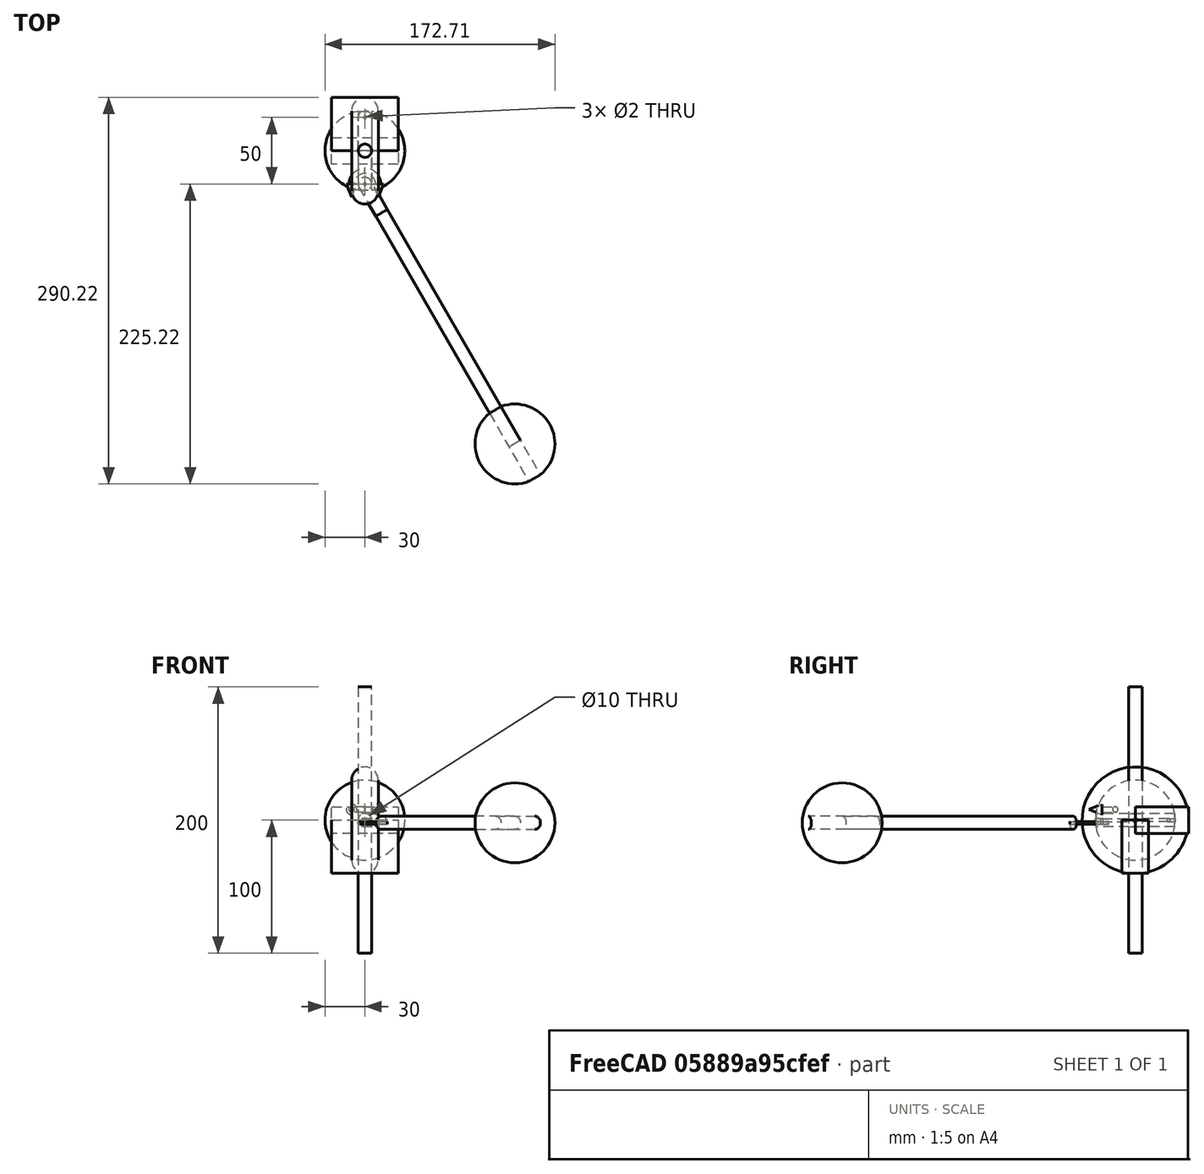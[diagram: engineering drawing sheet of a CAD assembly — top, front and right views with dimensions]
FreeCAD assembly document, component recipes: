
FREECAD ASSEMBLY — COMPONENT RECIPES ("NikraDAPBeginnersTutorial3")

This assembly document has 7 components, labeled P0..P6 below (a component is one placed body or linked part). 6 of them carry a construction recipe — the FreeCAD feature program that regenerates the part from scratch, quoted from this document or its linked companion documents; the rest are supplied as boundary geometry only. No exploded tour is included for this assembly.
COMPONENT P0 — recipe-attached ("LugBody", modeled in this document).
Construction recipe (the document's own serialized feature program — sketch geometry with constraints, then the solid features built on it; lengths are millimeters unless a unit is written):

FEATURE [Sketcher::SketchObject] Sketch
  FullyConstrained = true
  MapMode = 5
  Support = -> [XY_Plane]
  sketch-geometry (5):
    g0: LineSegment StartX=-5 StartY=0 StartZ=0 EndX=-5 EndY=25 EndZ=0
    g1: LineSegment StartX=5 StartY=25 StartZ=0 EndX=5 EndY=0 EndZ=0
    g2: LineSegment StartX=5 StartY=0 StartZ=0 EndX=-5 EndY=0 EndZ=0
    g3: Circle CenterX=0 CenterY=25 CenterZ=0 NormalX=0 NormalY=0 NormalZ=1 AngleXU=0 Radius=1
    g4: ArcOfCircle CenterX=0 CenterY=25 CenterZ=0 NormalX=0 NormalY=0 NormalZ=1 AngleXU=0 Radius=5 StartAngle=5e-16 EndAngle=3.1416
  constraints (13):
    c: PointOnObject(g0,g-1)
    c: Vertical(g0)
    c: Coincident(g1,g2)
    c: Coincident(g2,g0)
    c: Vertical(g1)
    c: Symmetric(g0,g1,g-1)
    c: Radius(g3) = 1
    c: Distance(g1) = 25
    c: Coincident(g4,g3)
    c: Coincident(g4,g0)
    c: Radius(g4) = 5
    c: Tangent(g4,g1) = 1.5708
    c: PointOnObject(g3,g-2)
FEATURE [PartDesign::Pad] Pad004
  Direction = (0,0,1)
  Length = 2
  Length2 = 10
  Midplane = true
  Profile = -> Sketch
  ReferenceAxis = -> Sketch [N_Axis]
  Type = 0
FEATURE [PartDesign::CoordinateSystem] LugFace
  AttacherType = Attacher::AttachEngine3D
  MapMode = 5
  Placement = pos=(0,0,0) rot=(1,0,0;1.5708rad)
  Support = -> [Pad004]
FEATURE [PartDesign::CoordinateSystem] LugHole
  AttacherType = Attacher::AttachEngine3D
  MapMode = 11
  Placement = pos=(0,25,1) rot=(0,0,1;1.5708rad)
  Support = -> [Pad004]
FEATURE [PartDesign::CoordinateSystem] LugHoleRot
  AttacherType = Attacher::AttachEngine3D
  AttachmentOffset = pos=(0,0,0) rot=(0,0,1;0.523599rad)
  MapMode = 11
  Placement = pos=(0,25,1) rot=(0,0,1;2.0944rad)
  Support = -> [Pad004]
FEATURE [PartDesign::Body] Body  label="LugBody"
  Group = -> [Sketch,Pad004,LugFace,LugHole,LugHoleRot]
  Origin = -> Origin
  Tip = -> Pad004
COMPONENT P1 — recipe-attached ("RodBody", modeled in this document).
Construction recipe (the document's own serialized feature program — sketch geometry with constraints, then the solid features built on it; lengths are millimeters unless a unit is written):

FEATURE [Sketcher::SketchObject] Sketch001
  FullyConstrained = true
  MapMode = 5
  Support = -> [XY_Plane001]
  sketch-geometry (1):
    g0: Circle CenterX=0 CenterY=0 CenterZ=0 NormalX=0 NormalY=0 NormalZ=1 AngleXU=0 Radius=5
  constraints (2):
    c: Coincident(g0,g-1)
    c: Radius(g0) = 5
FEATURE [PartDesign::Pad] Pad
  Direction = (0,0,1)
  Length = 200
  Length2 = 10
  Midplane = true
  Profile = -> Sketch001
  ReferenceAxis = -> Sketch001 [N_Axis]
  Type = 0
FEATURE [PartDesign::CoordinateSystem] RodTop
  AttacherType = Attacher::AttachEngine3D
  MapMode = 11
  Placement = pos=(0,0,100) rot=(0,0,1;1.5708rad)
  Support = -> [Pad]
FEATURE [PartDesign::CoordinateSystem] RodBot
  AttacherType = Attacher::AttachEngine3D
  MapMode = 11
  Placement = pos=(0,0,-100) rot=(0,0,1;1.5708rad)
  Support = -> [Pad]
FEATURE [PartDesign::Body] Body001  label="RodBody"
  Group = -> [Sketch001,Pad,RodTop,RodBot]
  Origin = -> Origin001
  Tip = -> Pad
COMPONENT P2 — recipe-attached ("BobBody", modeled in this document).
Construction recipe (the document's own serialized feature program — sketch geometry with constraints, then the solid features built on it; lengths are millimeters unless a unit is written):

FEATURE [Sketcher::SketchObject] Sketch004
  FullyConstrained = true
  MapMode = 5
  Support = -> [XY_Plane004]
  sketch-geometry (4):
    g0: LineSegment StartX=-10 StartY=0 StartZ=0 EndX=-10 EndY=30 EndZ=0
    g1: ArcOfCircle CenterX=0 CenterY=30 CenterZ=0 NormalX=0 NormalY=0 NormalZ=1 AngleXU=0 Radius=10 StartAngle=2e-16 EndAngle=3.14159
    g2: LineSegment StartX=10 StartY=30 StartZ=0 EndX=10 EndY=0 EndZ=0
    g3: LineSegment StartX=10 StartY=0 StartZ=0 EndX=-10 EndY=0 EndZ=0
  constraints (11):
    c: PointOnObject(g0,g-1)
    c: Vertical(g0)
    c: Tangent(g0,g1) = 1.5708
    c: Tangent(g1,g2) = 1.5708
    c: Coincident(g2,g3)
    c: Coincident(g3,g0)
    c: Vertical(g2)
    c: PointOnObject(g1,g-2)
    c: Diameter(g1) = 20
    c: Distance(g0) = 30
    c: PointOnObject(g2,g-1)
FEATURE [PartDesign::Revolution] Revolution001
  Angle = 360
  Axis = (1,0,0)
  Base = (0,0,0)
  Profile = -> Sketch004
  ReferenceAxis = -> Sketch004 [H_Axis]
FEATURE [PartDesign::CoordinateSystem] BobSurface
  AttacherType = Attacher::AttachEngine3D
  MapMode = 11
  Placement = pos=(10,-3.6e-15,0) rot=(0.707107,0,0.707107;3.14159rad)
  Support = -> [Revolution001]
FEATURE [PartDesign::Body] Body004  label="BobBody"
  Group = -> [Sketch004,Revolution001,BobSurface]
  Origin = -> Origin004
  Tip = -> Revolution001
COMPONENT P3 — recipe-attached ("GroundBody", modeled in this document).
Construction recipe (the document's own serialized feature program — sketch geometry with constraints, then the solid features built on it; lengths are millimeters unless a unit is written):

FEATURE [Sketcher::SketchObject] Sketch005
  FullyConstrained = true
  MapMode = 5
  Support = -> [XY_Plane005]
  sketch-geometry (4):
    g0: LineSegment StartX=-25 StartY=10 StartZ=0 EndX=25 EndY=10 EndZ=0
    g1: LineSegment StartX=25 StartY=10 StartZ=0 EndX=25 EndY=-10 EndZ=0
    g2: LineSegment StartX=25 StartY=-10 StartZ=0 EndX=-25 EndY=-10 EndZ=0
    g3: LineSegment StartX=-25 StartY=-10 StartZ=0 EndX=-25 EndY=10 EndZ=0
  constraints (11):
    c: Coincident(g0,g1)
    c: Coincident(g1,g2)
    c: Coincident(g2,g3)
    c: Coincident(g3,g0)
    c: Horizontal(g0)
    c: Horizontal(g2)
    c: Vertical(g1)
    c: Vertical(g3)
    c: DistanceY(g2,g0) = 20
    c: DistanceX(g0,g0) = 50
    c: Symmetric(g0,g1,g-1)
FEATURE [PartDesign::Pad] Pad003
  Direction = (0,0,1)
  Length = 40
  Length2 = 10
  Profile = -> Sketch005
  ReferenceAxis = -> Sketch005 [N_Axis]
  Reversed = true
  Type = 0
FEATURE [PartDesign::CoordinateSystem] GroundFace
  AttacherType = Attacher::AttachEngine3D
  MapMode = 5
  Support = -> [Pad003]
FEATURE [PartDesign::Body] Body005  label="GroundBody"
  Group = -> [Sketch005,Pad003,GroundFace]
  Origin = -> Origin005
  Tip = -> Pad003
COMPONENT P4 — recipe-attached ("ShortRodBody", modeled in this document).
Construction recipe (the document's own serialized feature program — sketch geometry with constraints, then the solid features built on it; lengths are millimeters unless a unit is written):

FEATURE [Sketcher::SketchObject] Sketch006
  FullyConstrained = true
  MapMode = 5
  Support = -> [XY_Plane007]
  sketch-geometry (1):
    g0: Circle CenterX=0 CenterY=0 CenterZ=0 NormalX=0 NormalY=0 NormalZ=1 AngleXU=0 Radius=5
  constraints (2):
    c: Coincident(g0,g-1)
    c: Radius(g0) = 5
FEATURE [PartDesign::Pad] Pad005
  Direction = (0,0,1)
  Length = 10
  Length2 = 10
  Midplane = true
  Profile = -> Sketch006
  ReferenceAxis = -> Sketch006 [N_Axis]
  Type = 0
FEATURE [PartDesign::CoordinateSystem] MiniRodTop
  AttacherType = Attacher::AttachEngine3D
  MapMode = 11
  Placement = pos=(0,0,5) rot=(0,0,1;1.5708rad)
  Support = -> [Pad005]
FEATURE [PartDesign::CoordinateSystem] MiniRodBot
  AttacherType = Attacher::AttachEngine3D
  MapMode = 11
  Placement = pos=(0,0,-5) rot=(0,0,1;1.5708rad)
  Support = -> [Pad005]
FEATURE [PartDesign::Body] Body006  label="ShortRodBody"
  Group = -> [Sketch006,Pad005,MiniRodTop,MiniRodBot]
  Origin = -> Origin007
  Tip = -> Pad005
COMPONENT P5 — recipe-attached ("Weight", modeled in this document).
Construction recipe (the document's own serialized feature program — sketch geometry with constraints, then the solid features built on it; lengths are millimeters unless a unit is written):

FEATURE [Sketcher::SketchObject] Sketch007
  FullyConstrained = true
  MapMode = 5
  Support = -> [XY_Plane009]
  sketch-geometry (2):
    g0: ArcOfCircle CenterX=0 CenterY=0 CenterZ=0 NormalX=0 NormalY=0 NormalZ=1 AngleXU=0 Radius=30 StartAngle=1.73824 EndAngle=4.54494
    g1: LineSegment StartX=-5 StartY=29.5804 StartZ=0 EndX=-5 EndY=-29.5804 EndZ=0
  constraints (6):
    c: Vertical(g1)
    c: Coincident(g0,g1)
    c: Coincident(g0,g1)
    c: Radius(g0) = 30
    c: Coincident(g0,g-1)
    c: DistanceX(g0,g0) = 5
FEATURE [PartDesign::Revolution] Revolution
  Angle = 360
  Axis = (0,1,0)
  Base = (0,0,0)
  Profile = -> Sketch007
  ReferenceAxis = -> Sketch007 [V_Axis]
FEATURE [PartDesign::CoordinateSystem] WeightOrigin
  AttacherType = Attacher::AttachEngine3D
  AttachmentOffset = pos=(0,0,30) rot=(0,0,1;0rad)
  MapMode = 11
  Placement = pos=(0,0.419601,0) rot=(0.57735,0.57735,0.57735;4.18879rad)
  Support = -> [Revolution]
FEATURE [PartDesign::Body] Body007  label="Weight"
  Group = -> [Sketch007,Revolution,WeightOrigin]
  Origin = -> Origin009
  Tip = -> Revolution
COMPONENT P6 — geometry summary ("Model"; no construction recipe available for this part):
  bounding box: 290.2 x 167.7 x 60.0 mm
  tessellated surface: 9,208 triangles
  volume: 165270 mm^3 (6% of its bounding box)
PROVENANCE & LICENSES
A FreeCAD (.FCStd) document from a public repository crawl; recipes are the document's own serialized feature recipes (and, for linked parts, companion documents' recipes).
License: gpl-3.0.
